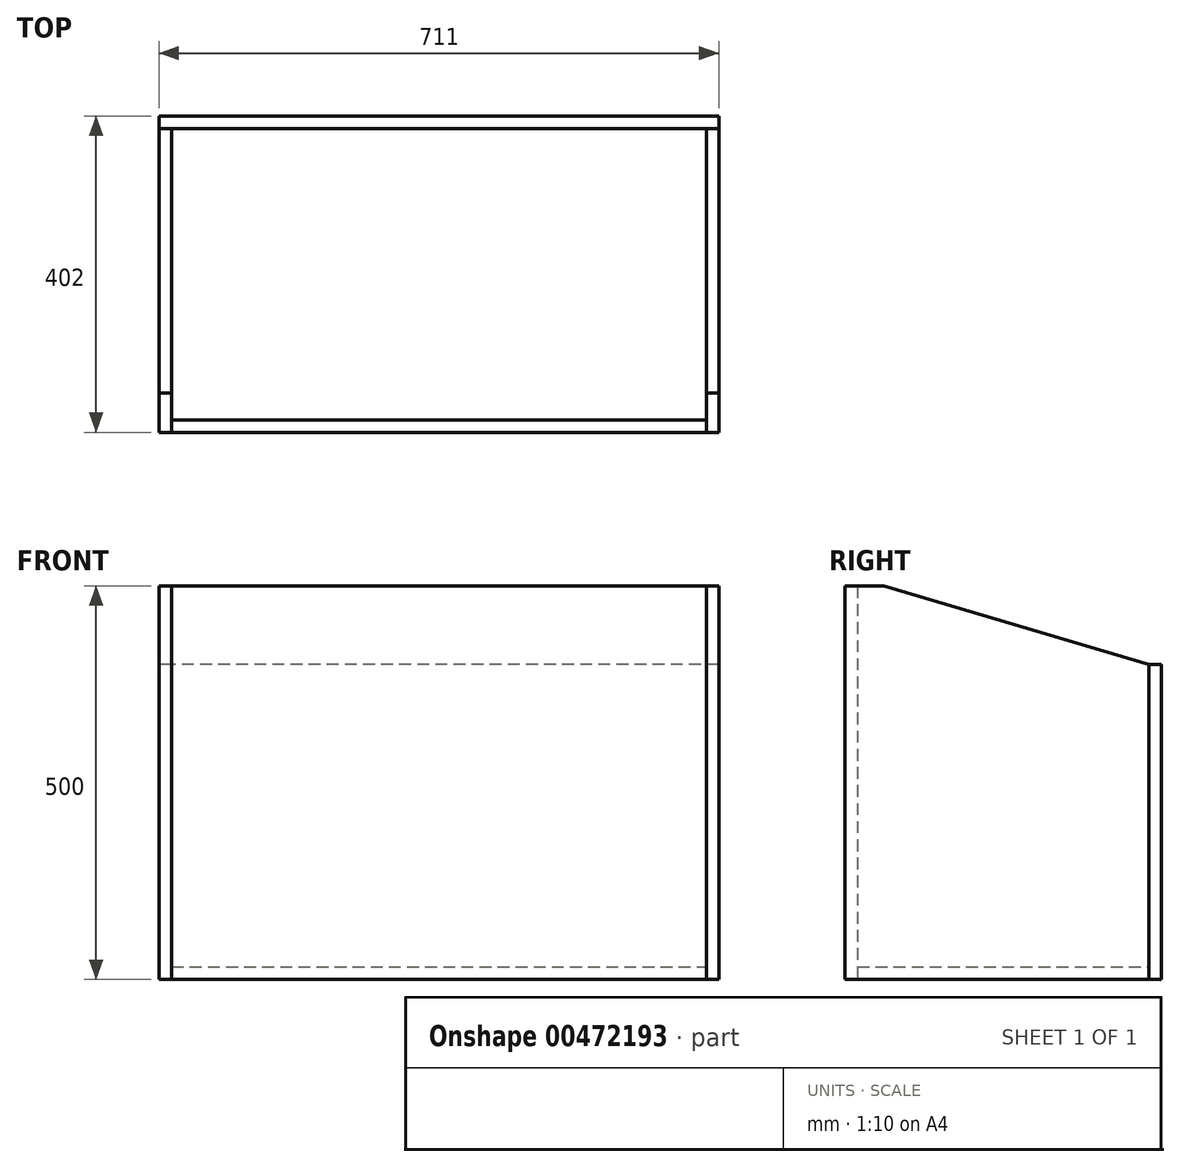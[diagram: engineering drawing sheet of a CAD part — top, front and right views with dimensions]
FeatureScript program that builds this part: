
annotation { "Feature Type Name" : "Feature", "Feature Type Description" : "" }
export const myFeature = defineFeature(function(context is Context, id is Id, definition is map)
    precondition{}
    {
        {
            var Q0;
            Q0=qCreatedBy(makeId("Top.planeOp"),FACE);
            var sketch = newSketch(context, id + "F0", { "sketchPlane" : qUnion([Q0])});
            skLineSegment(sketch, "E0.bottom", {"start": v(0, 0) * mm, "end": v(679, 0) * mm});
            skLineSegment(sketch, "E0.top", {"start": v(0, 370) * mm, "end": v(679, 370) * mm});
            skLineSegment(sketch, "E0.left", {"start": v(0, 0) * mm, "end": v(0, 370) * mm});
            skLineSegment(sketch, "E0.right", {"start": v(679, 0) * mm, "end": v(679, 370) * mm});
            skSolve(sketch);
        }
        {
            var Q0;
            Q0 = qSketchRegion(id + "F0", true);
            extrude(context, id + "F1", {"entities" : qUnion([Q0]), "depth" : 16 * mm});
        }
        {
            var Q0;
            Q0=makeQuery(id+"F1.opExtrude","SWEPT_FACE",FACE,{"disambiguationData":[OSD([sQuery(id+"F0.wireOp",EDGE,"E0.bottom")])]});
            var sketch = newSketch(context, id + "F2", { "sketchPlane" : qUnion([Q0])});
            skLineSegment(sketch, "E1.bottom", {"start": v(0, 0) * mm, "end": v(679, 0) * mm});
            skLineSegment(sketch, "E1.top", {"start": v(0, 500) * mm, "end": v(679, 500) * mm});
            skLineSegment(sketch, "E1.left", {"start": v(0, 0) * mm, "end": v(0, 500) * mm});
            skLineSegment(sketch, "E1.right", {"start": v(679, 0) * mm, "end": v(679, 500) * mm});
            skSolve(sketch);
        }
        {
            var Q0;
            Q0 = qSketchRegion(id + "F2", true);
            extrude(context, id + "F3", {"entities" : qUnion([Q0]), "depth" : 16 * mm});
        }
        {
            var Q0;
            Q0=makeQuery(id+"F1.opExtrude","SWEPT_FACE",FACE,{"disambiguationData":[OSD([sQuery(id+"F0.wireOp",EDGE,"E0.right")])]});
            var sketch = newSketch(context, id + "F4", { "sketchPlane" : qUnion([Q0])});
            skLineSegment(sketch, "E2", {"start": v(-16, 500) * mm, "end": v(34, 500) * mm});
            skLineSegment(sketch, "E3", {"start": v(34, 500) * mm, "end": v(370, 400) * mm});
            skLineSegment(sketch, "E4", {"start": v(370, 400) * mm, "end": v(370, 0) * mm});
            skLineSegment(sketch, "E5", {"start": v(370, 0) * mm, "end": v(-16, 0) * mm});
            skLineSegment(sketch, "E6", {"start": v(-16, 0) * mm, "end": v(-16, 500) * mm});
            skSolve(sketch);
        }
        {
            var Q0;
            Q0 = qSketchRegion(id + "F4", true);
            extrude(context, id + "F5", {"entities" : qUnion([Q0]), "depth" : 16 * mm});
        }
        {
            var Q0;
            Q0=makeQuery(id+"F5.opExtrude","SWEPT_BODY",BODY,{"disambiguationData":[OSD([sQuery(id+"F4.wireOp",EDGE,"E2"),sQuery(id+"F4.wireOp",EDGE,"E3"),sQuery(id+"F4.wireOp",EDGE,"E4"),sQuery(id+"F4.wireOp",EDGE,"E5"),sQuery(id+"F4.wireOp",EDGE,"E6")])]});
            var Q1;
            Q1=makeQuery(id+"F1.opExtrude","CAP_EDGE",EDGE,{"disambiguationData":[OSD([sQuery(id+"F0.wireOp",EDGE,"E0.bottom")])],"isStart":false});
            transform(context, id + "F6", {"entities" : qUnion([Q0]), "transformType" : TransformType.TRANSLATION_DISTANCE, "transformDirection" : qUnion([Q1]), "distance" : 695 * mm, "oppositeDirection" : true, "makeCopy" : true});
        }
        {
            var Q0;
            Q0=makeQuery(id+"F5.opExtrude","SWEPT_FACE",FACE,{"disambiguationData":[OSD([sQuery(id+"F4.wireOp",EDGE,"E4")])]});
            var sketch = newSketch(context, id + "F7", { "sketchPlane" : qUnion([Q0])});
            skLineSegment(sketch, "E7.bottom", {"start": v(-695, 400) * mm, "end": v(16, 400) * mm});
            skLineSegment(sketch, "E7.top", {"start": v(-695, 0) * mm, "end": v(16, 0) * mm});
            skLineSegment(sketch, "E7.left", {"start": v(-695, 400) * mm, "end": v(-695, 0) * mm});
            skLineSegment(sketch, "E7.right", {"start": v(16, 400) * mm, "end": v(16, 0) * mm});
            skSolve(sketch);
        }
        {
            var Q0;
            Q0 = qSketchRegion(id + "F7", true);
            extrude(context, id + "F8", {"entities" : qUnion([Q0]), "depth" : 16 * mm});
        }
    });
